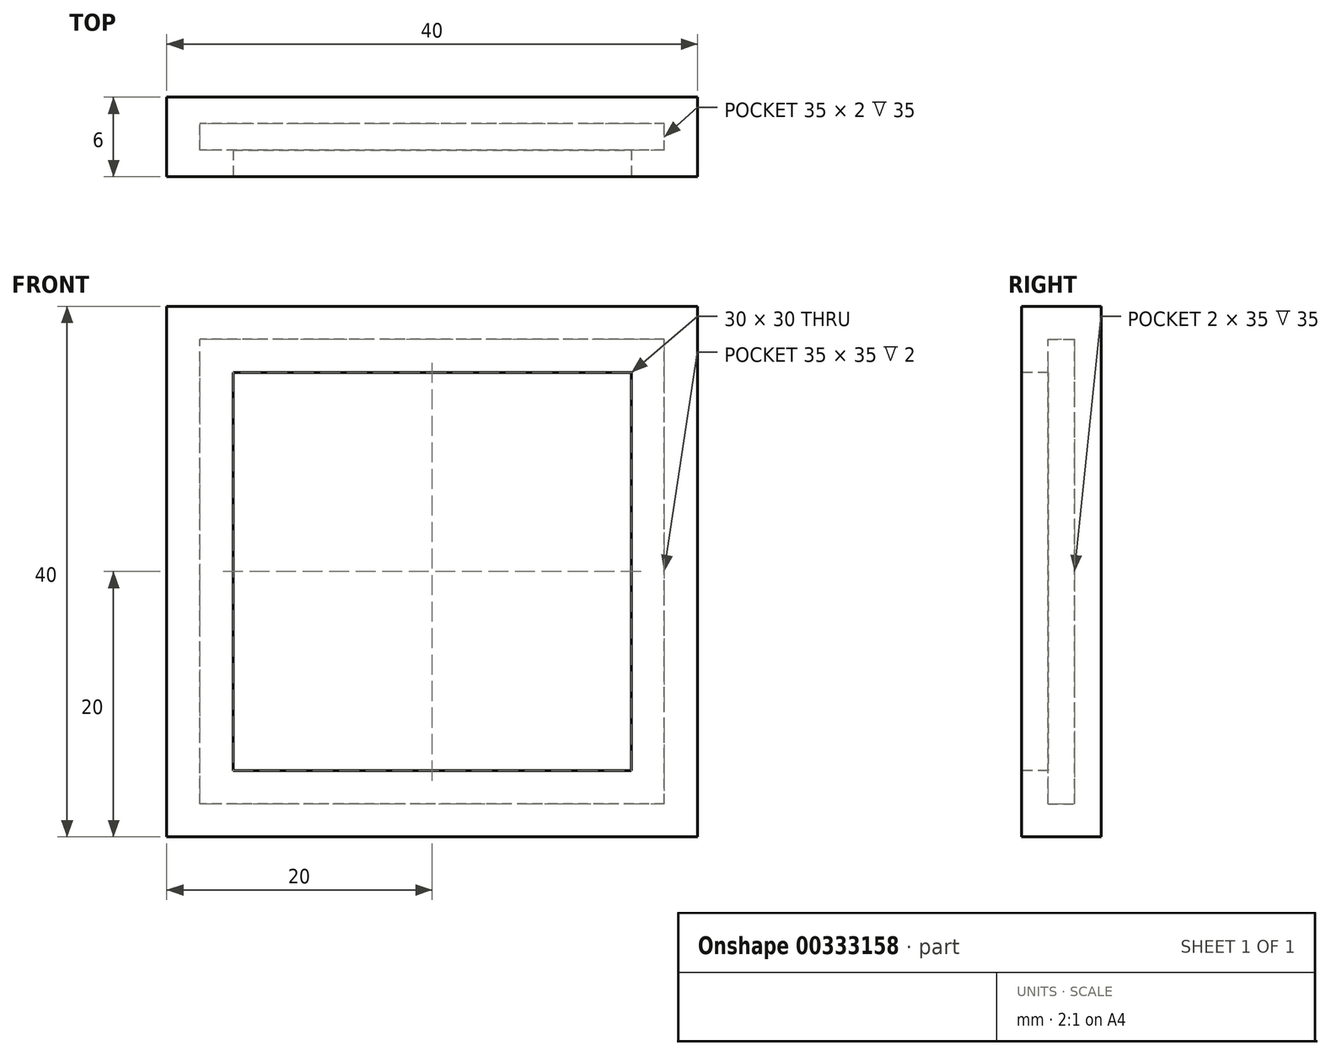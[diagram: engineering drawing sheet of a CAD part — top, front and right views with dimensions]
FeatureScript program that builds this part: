
annotation { "Feature Type Name" : "Feature", "Feature Type Description" : "" }
export const myFeature = defineFeature(function(context is Context, id is Id, definition is map)
    precondition{}
    {
        {
            var Q0;
            Q0=qCreatedBy(makeId("Front.planeOp"),FACE);
            var sketch = newSketch(context, id + "F0", { "sketchPlane" : qUnion([Q0])});
            skLineSegment(sketch, "E0.bottom", {"start": v(20, -20) * mm, "end": v(-20, -20) * mm});
            skLineSegment(sketch, "E0.top", {"start": v(20, 20) * mm, "end": v(-20, 20) * mm});
            skLineSegment(sketch, "E0.left", {"start": v(20, -20) * mm, "end": v(20, 20) * mm});
            skLineSegment(sketch, "E0.right", {"start": v(-20, -20) * mm, "end": v(-20, 20) * mm});
            skPoint(sketch, "E0.middle", {"position": v(0, 0) * mm});
            skLineSegment(sketch, "E1.bottom", {"start": v(17.5, -17.5) * mm, "end": v(-17.5, -17.5) * mm});
            skLineSegment(sketch, "E1.top", {"start": v(17.5, 17.5) * mm, "end": v(-17.5, 17.5) * mm});
            skLineSegment(sketch, "E1.left", {"start": v(17.5, -17.5) * mm, "end": v(17.5, 17.5) * mm});
            skLineSegment(sketch, "E1.right", {"start": v(-17.5, -17.5) * mm, "end": v(-17.5, 17.5) * mm});
            skSolve(sketch);
        }
        {
            var Q0;
            Q0=qSketchRegion(id+"F0",true);
            extrude(context, id + "F1", {"entities" : qUnion([Q0]), "depth" : 6 * mm});
        }
        {
            var Q0;
            Q0=makeQuery(id+"F0.imprint","IMPRINT",FACE,{"disambiguationData":[TD([[makeQuery(id+"F0.imprint","IMPRINT",EDGE,{"derivedFrom":sQuery(id+"F0.wireOp",EDGE,"E1.bottom")}),-1.0]])]});
            extrude(context, id + "F2", {"entities" : qUnion([Q0]), "operationType" : NewBodyOperationType.ADD, "depth" : 2 * mm});
        }
        {
            var Q0;
            Q0=makeQuery(id+"F1.opExtrude","CAP_FACE",FACE,{"disambiguationData":[OSD([sQuery(id+"F0.wireOp",EDGE,"E0.bottom"),sQuery(id+"F0.wireOp",EDGE,"E0.top"),sQuery(id+"F0.wireOp",EDGE,"E0.left"),sQuery(id+"F0.wireOp",EDGE,"E0.right"),sQuery(id+"F0.wireOp",EDGE,"E1.bottom"),sQuery(id+"F0.wireOp",EDGE,"E1.top"),sQuery(id+"F0.wireOp",EDGE,"E1.left"),sQuery(id+"F0.wireOp",EDGE,"E1.right")])],"isStart":false});
            var sketch = newSketch(context, id + "F3", { "sketchPlane" : qUnion([Q0])});
            skLineSegment(sketch, "E2", {"start": v(-17.5, 15) * mm, "end": v(17.5, 15) * mm});
            skLineSegment(sketch, "E3", {"start": v(15, 15) * mm, "end": v(15, -20) * mm});
            skLineSegment(sketch, "E4", {"start": v(15, -15) * mm, "end": v(-20, -15) * mm});
            skLineSegment(sketch, "E5", {"start": v(-15, -15) * mm, "end": v(-15, 15) * mm});
            skSolve(sketch);
        }
        {
            var Q0;
            {var subQ0=makeQuery(id+"F1.opExtrude","CAP_EDGE",EDGE,{"disambiguationData":[OSD([sQuery(id+"F0.wireOp",EDGE,"E1.top")])],"isStart":false});Q0=makeQuery(id+"F3.imprint","IMPRINT",FACE,{"disambiguationData":[TD([[makeQuery(id+"F3.imprint","IMPRINT",EDGE,{"derivedFrom":subQ0}),1.0]])]});}
            var Q1;
            {var subQ3=sQuery(id+"F3.wireOp",EDGE,"E5");Q1=makeQuery(id+"F3.imprint","IMPRINT",FACE,{"disambiguationData":[TD([[makeQuery(id+"F3.imprint","IMPRINT",EDGE,{"derivedFrom":subQ3}),1.0]])]});}
            var Q2;
            {var subQ3=sQuery(id+"F3.wireOp",EDGE,"E3");var subQ5=sQuery(id+"F3.wireOp",EDGE,"E4");var subQ8=makeQuery(id+"F3.imprint","INTERSECT",VERTEX,{"derivedFrom":[subQ3,subQ5]});Q2=makeQuery(id+"F3.imprint","IMPRINT",FACE,{"disambiguationData":[TD([[makeQuery(id+"F3.imprint","IMPRINT",EDGE,{"disambiguationData":[TD([[subQ8,-1.0]])],"derivedFrom":subQ3}),-1.0]])]});}
            var Q3;
            {var subQ4=sQuery(id+"F3.wireOp",EDGE,"E2");var subQ6=makeQuery(id+"F1.opExtrude","CAP_EDGE",EDGE,{"disambiguationData":[OSD([sQuery(id+"F0.wireOp",EDGE,"E1.left")])],"isStart":false});var subQ8=makeQuery(id+"F3.imprint","INTERSECT",VERTEX,{"derivedFrom":[subQ6,subQ4]});Q3=makeQuery(id+"F3.imprint","IMPRINT",FACE,{"disambiguationData":[TD([[makeQuery(id+"F3.imprint","IMPRINT",EDGE,{"disambiguationData":[TD([[subQ8,1.0]])],"derivedFrom":subQ4}),-1.0]])]});}
            extrude(context, id + "F4", {"entities" : qUnion([Q0, Q1, Q2, Q3]), "operationType" : NewBodyOperationType.ADD, "oppositeDirection" : true, "depth" : 2 * mm});
        }
    });
